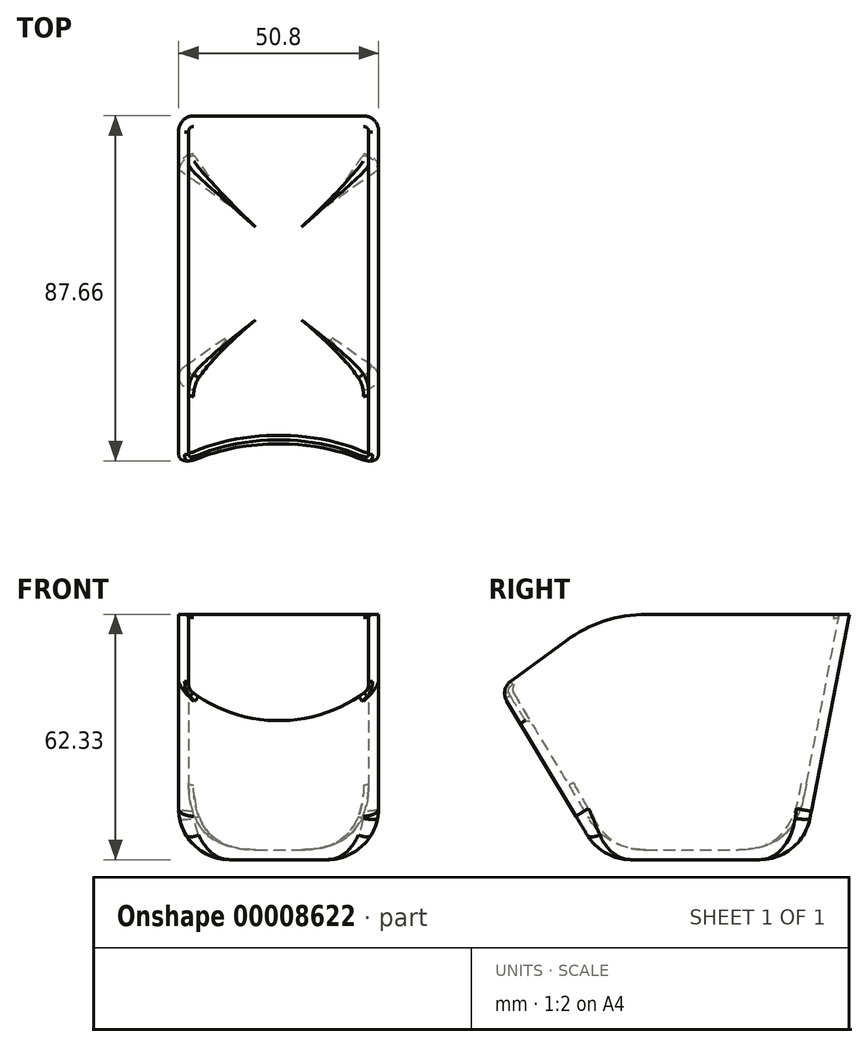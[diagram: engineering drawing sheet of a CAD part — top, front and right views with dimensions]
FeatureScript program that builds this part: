
annotation { "Feature Type Name" : "Feature", "Feature Type Description" : "" }
export const myFeature = defineFeature(function(context is Context, id is Id, definition is map)
    precondition{}
    {
        {
            var Q0;
            Q0=qCreatedBy(makeId("Right.planeOp"),FACE);
            var sketch = newSketch(context, id + "F0", { "sketchPlane" : qUnion([Q0])});
            skLineSegment(sketch, "E0", {"start": v(0, 0) * mm, "end": v(-25.98, 43.28) * mm});
            skLineSegment(sketch, "E1", {"start": v(62.92, 62.33) * mm, "end": v(50.8, 0) * mm});
            skLineSegment(sketch, "E2", {"start": v(50.8, 0) * mm, "end": v(0, 0) * mm});
            skLineSegment(sketch, "E3", {"start": v(62.92, 62.33) * mm, "end": v(11.36, 62.33) * mm});
            skLineSegment(sketch, "E4", {"start": v(-9.16, 55.62) * mm, "end": v(-25.98, 43.28) * mm});
            skArc(sketch, "E5", {"start": v(32.38, 0) * mm, "mid": v(35.24, 2.43) * mm, "end": v(37.82, 5.15) * mm});
            skPoint(sketch, "E5.first.point", {"position": v(-9.16, 55.62) * mm});
            skPoint(sketch, "E5.second.point", {"position": v(11.36, 62.33) * mm});
            skPoint(sketch, "E5.third.point", {"position": v(37.82, 5.15) * mm});
            skArc(sketch, "E6.trimOffspring", {"start": v(11.36, 62.33) * mm, "mid": v(0.56, 60.61) * mm, "end": v(-9.16, 55.62) * mm});
            skPoint(sketch, "E7.orphan", {"position": v(0, 62.33) * mm});
            skSolve(sketch);
        }
        {
            var Q0;
            Q0=makeQuery(id+"F0.imprint","IMPRINT",FACE,{"disambiguationData":[TD([[makeQuery(id+"F0.imprint","IMPRINT",EDGE,{"derivedFrom":sQuery(id+"F0.wireOp",EDGE,"E0")}),-1.0]])]});
            extrude(context, id + "F1", {"entities" : qUnion([Q0]), "depth" : 25.4 * mm, "hasSecondDirection" : true, "secondDirectionOppositeDirection" : true, "secondDirectionDepth" : 25.4 * mm});
        }
        {
            var Q0;
            Q0=makeQuery(id+"F1.opExtrude","SWEPT_FACE",FACE,{"disambiguationData":[OSD([sQuery(id+"F0.wireOp",EDGE,"E3")])]});
            var Q1;
            Q1=makeQuery(id+"F1.opExtrude","SWEPT_FACE",FACE,{"disambiguationData":[OSD([sQuery(id+"F0.wireOp",EDGE,"E4")])]});
            var Q2;
            Q2=makeQuery(id+"F1.opExtrude","SWEPT_FACE",FACE,{"disambiguationData":[OSD([sQuery(id+"F0.wireOp",EDGE,"E6.trimOffspring")])]});
            shell(context, id + "F2", {"entities" : qUnion([Q0, Q1, Q2]), "thickness" : 2.54 * mm});
        }
        {
            var Q0;
            Q0=qCreatedBy(makeId("Front.planeOp"),FACE);
            var sketch = newSketch(context, id + "F3", { "sketchPlane" : qUnion([Q0])});
            skPoint(sketch, "E8.first.point", {"position": v(-22.86, 45.07) * mm});
            skPoint(sketch, "E8.second.point", {"position": v(22.86, 45.07) * mm});
            skPoint(sketch, "E8.third.point", {"position": v(0, 75.7) * mm});
            skLineSegment(sketch, "E9", {"start": v(-22.86, 45.07) * mm, "end": v(22.86, 45.07) * mm});
            skLineSegment(sketch, "E10", {"start": v(-22.86, 45.07) * mm, "end": v(-22.86, 43.28) * mm});
            skLineSegment(sketch, "E11", {"start": v(22.86, 45.07) * mm, "end": v(22.86, 43.28) * mm});
            skArc(sketch, "E12", {"start": v(-22.86, 43.28) * mm, "mid": v(0, 35.29) * mm, "end": v(22.86, 43.28) * mm});
            skSolve(sketch);
        }
        {
            var Q0;
            Q0 = qSketchRegion(id + "F3", true);
            extrude(context, id + "F4", {"entities" : qUnion([Q0]), "operationType" : NewBodyOperationType.REMOVE, "endBound" : BoundingType.THROUGH_ALL, "depth" : 25.4 * mm});
        }
        {
            var Q0;
            Q0=makeQuery(id+"F4.boolean.opBoolean","COPY",EDGE,{"derivedFrom":makeQuery(id+"F4.opExtrude","SWEPT_EDGE",EDGE,{"disambiguationData":[OSD([sQuery(id+"F3.wireOp",EDGE,"E10"),sQuery(id+"F3.wireOp",EDGE,"E12")])]})});
            var Q1;
            Q1=makeQuery(id+"F4.boolean.opBoolean","COPY",EDGE,{"derivedFrom":makeQuery(id+"F4.opExtrude","SWEPT_EDGE",EDGE,{"disambiguationData":[OSD([sQuery(id+"F3.wireOp",EDGE,"E11"),sQuery(id+"F3.wireOp",EDGE,"E12")])]})});
            fillet(context, id + "F5", {"entities" : qUnion([Q0, Q1]), "radius" : 2.54 * mm, "tangentPropagation" : true, "allowEdgeOverflow" : false});
        }
        {
            var Q0;
            Q0=makeQuery(id+"F1.opExtrude","CAP_EDGE",EDGE,{"disambiguationData":[OSD([sQuery(id+"F0.wireOp",EDGE,"E0")])],"isStart":false});
            var Q1;
            Q1=makeQuery(id+"F1.opExtrude","CAP_EDGE",EDGE,{"disambiguationData":[OSD([sQuery(id+"F0.wireOp",EDGE,"E0")])],"isStart":true});
            var Q2;
            Q2=makeQuery(id+"F1.opExtrude","CAP_EDGE",EDGE,{"disambiguationData":[OSD([sQuery(id+"F0.wireOp",EDGE,"E1")])],"isStart":false});
            var Q3;
            Q3=makeQuery(id+"F1.opExtrude","CAP_EDGE",EDGE,{"disambiguationData":[OSD([sQuery(id+"F0.wireOp",EDGE,"E1")])],"isStart":true});
            var Q4;
            {var subQ0=sQuery(id+"F0.wireOp",EDGE,"E0");var subQ1=sQuery(id+"F0.wireOp",EDGE,"E4");Q4=makeQuery(id+"F4.boolean.opBoolean","SPLIT",EDGE,{"disambiguationData":[TD([makeQuery(id+"F4.opExtrude","SWEPT_FACE",FACE,{"disambiguationData":[OSD([sQuery(id+"F3.wireOp",EDGE,"E10")])]})])],"derivedFrom":makeQuery(id+"F1.opExtrude","SWEPT_EDGE",EDGE,{"disambiguationData":[OSD([subQ0,subQ1])]})});}
            var Q5;
            {var subQ0=sQuery(id+"F0.wireOp",EDGE,"E0");var subQ1=sQuery(id+"F0.wireOp",EDGE,"E4");Q5=makeQuery(id+"F4.boolean.opBoolean","SPLIT",EDGE,{"disambiguationData":[TD([makeQuery(id+"F4.opExtrude","SWEPT_FACE",FACE,{"disambiguationData":[OSD([sQuery(id+"F3.wireOp",EDGE,"E11")])]})])],"derivedFrom":makeQuery(id+"F1.opExtrude","SWEPT_EDGE",EDGE,{"disambiguationData":[OSD([subQ0,subQ1])]})});}
            fillet(context, id + "F6", {"entities" : qUnion([Q0, Q1, Q2, Q3, Q4, Q5]), "radius" : 3.8 * mm, "tangentPropagation" : true, "allowEdgeOverflow" : false});
        }
        {
            var Q0;
            {var subQ0=sQuery(id+"F0.wireOp",EDGE,"E1");Q0=makeQuery(id+"F2.opShell","OFFSET_EDGE",EDGE,{"disambiguationData":[OSD([subQ0]),TDD([makeQuery(id+"F1.opExtrude","CAP_EDGE",EDGE,{"disambiguationData":[OSD([subQ0])],"isStart":true})])]});}
            var Q1;
            {var subQ0=sQuery(id+"F0.wireOp",EDGE,"E1");Q1=makeQuery(id+"F2.opShell","OFFSET_EDGE",EDGE,{"disambiguationData":[OSD([subQ0]),TDD([makeQuery(id+"F1.opExtrude","CAP_EDGE",EDGE,{"disambiguationData":[OSD([subQ0])],"isStart":false})])]});}
            var Q2;
            {var subQ0=sQuery(id+"F0.wireOp",EDGE,"E0");Q2=makeQuery(id+"F2.opShell","OFFSET_EDGE",EDGE,{"disambiguationData":[OSD([subQ0]),TDD([makeQuery(id+"F1.opExtrude","CAP_EDGE",EDGE,{"disambiguationData":[OSD([subQ0])],"isStart":true})])]});}
            var Q3;
            {var subQ0=sQuery(id+"F0.wireOp",EDGE,"E0");Q3=makeQuery(id+"F2.opShell","OFFSET_EDGE",EDGE,{"disambiguationData":[OSD([subQ0]),TDD([makeQuery(id+"F1.opExtrude","CAP_EDGE",EDGE,{"disambiguationData":[OSD([subQ0])],"isStart":false})])]});}
            fillet(context, id + "F7", {"entities" : qUnion([Q0, Q1, Q2, Q3]), "radius" : 1.27 * mm, "tangentPropagation" : true, "rho" : 0.5, "crossSection" : FilletCrossSection.CONIC, "allowEdgeOverflow" : false});
        }
        {
            var Q0;
            Q0=makeQuery(id+"F2.opShell","OFFSET_EDGE",EDGE,{"disambiguationData":[OSD([sQuery(id+"F0.wireOp",EDGE,"E0"),sQuery(id+"F0.wireOp",EDGE,"E2")])]});
            var Q1;
            Q1=makeQuery(id+"F2.opShell","OFFSET_EDGE",EDGE,{"disambiguationData":[OSD([sQuery(id+"F0.wireOp",EDGE,"E1"),sQuery(id+"F0.wireOp",EDGE,"E2")])]});
            fillet(context, id + "F8", {"entities" : qUnion([Q0, Q1]), "radius" : 17 * mm, "tangentPropagation" : true, "rho" : 0.5, "crossSection" : FilletCrossSection.CONIC, "allowEdgeOverflow" : false});
        }
        {
            var Q0;
            Q0=makeQuery(id+"F1.opExtrude","SWEPT_EDGE",EDGE,{"disambiguationData":[OSD([sQuery(id+"F0.wireOp",EDGE,"E1"),sQuery(id+"F0.wireOp",EDGE,"E2")])]});
            fillet(context, id + "F9", {"entities" : qUnion([Q0]), "radius" : 13 * mm, "tangentPropagation" : true, "allowEdgeOverflow" : false});
        }
        {
            var Q0;
            {var subQ0=sQuery(id+"F0.wireOp",EDGE,"E3");Q0=makeQuery(id+"F2.opShell","OFFSET_EDGE",EDGE,{"disambiguationData":[OSD([subQ0]),TDD([makeQuery(id+"F1.opExtrude","CAP_EDGE",EDGE,{"disambiguationData":[OSD([subQ0])],"isStart":true})])]});}
            fillet(context, id + "F10", {"entities" : qUnion([Q0]), "radius" : 1 * mm, "tangentPropagation" : true, "allowEdgeOverflow" : false});
        }
    });
